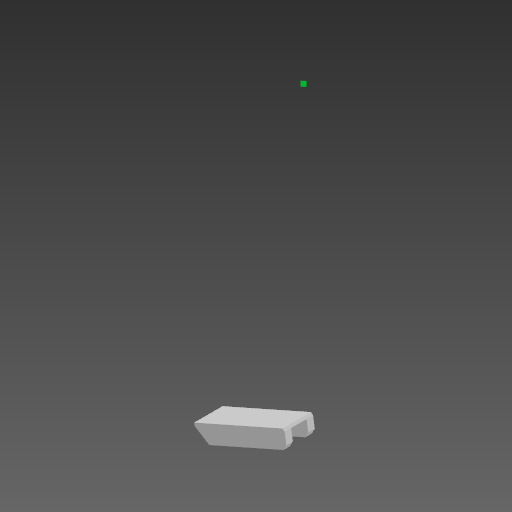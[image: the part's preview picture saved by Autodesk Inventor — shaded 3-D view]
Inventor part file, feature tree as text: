
AUTODESK INVENTOR PART (.ipt)
format: ipt  version: 2020 (Build 240168000, 168)  size: 99,840 bytes
history: native  units: in
note: dims shown in document units (in); Inventor stores cm internally (conversion verified against a paired STEP export)
features: sketch x3, extrude x2, plane x1
ambient origin geometry x8: Origin, YZ Plane, XZ Plane, XY Plane, X Axis, Y Axis, Z Axis, Center Point
bodies: Solid1 (feature_tree)
feature tree (6):
  extrude  "Extrusion1"  Depth=1.75in TaperAngle=0.0deg
  sketch  "Sketch2"  dims[d12=1.0in d13=0.0in]
  plane  "Work Plane1"
  extrude  "Extrusion2"  [1 undecoded]
  sketch  "Sketch4"
  sketch  "Sketch1"  dims[d3=0.15in d6=5.25in d8=0.25in d9=0.25in d10=1.75in d11=0.0in]
note: 1 required parameter value undecoded (feature->parameter linkage not recoverable at this tier; creation-order binding heuristic only, values carry confidence <= 0.55)
